# Revit family: 0048803 Sylvania Lighting Fixture HYDROPROOF LED G3 1500MM T 4K E3
name_source: partatom
category: Lighting Fixtures
revit_build: Autodesk Revit 2016 (Build: 20150220_1215(x64)
units: mm (PartAtom-declared; Revit-internal decimal feet)

## family parameters
Cut with Voids When Loaded = No
Host = Face
Light Source = Yes
OmniClass Number = 23.80.70.11.14
OmniClass Title = General Luminaries, Directional
Part Type = Normal
Room Calculation Point = No
Round Connector Dimension = Use Diameter
Shared = No

## types (2) — shared parameters
AccessoryMaterial = Diffuser-Sylvania-Glow
Assembly Code = D5020200
AssetType = Fixed
BodyMaterial = Body-Sylvania-Gray
ClassificationName = Uniclass2015
ClassificationValue = EF_70_80
Color Filter = 16777215
Default Elevation = 1219 mm
Description = Hydroproof, integrated LED chemical resistant weatherproof luminaire, with UV stabilized flat diffuser and linear prisms designed to achieve uniform lit appearance, optimise light output and to reduce glare, stainless steel diffuser clips and fixing brackets for surface and wall mounting. L 1578 mm x W 110 mm x H 78 mm size, GRP housing, PMMA diffuser, Non dimmable,   3 hour emergency, 4000K, CRI80,  6900 lm, 49 W, 140 lm/W, nominal average life (h):50000, energy class: A++ A+ A Class I,IK02, IP65.
DiffuserMaterial = Diffuser-Sylvania-Transparent
Dimming Lamp Color Temperature Shift = <None>
DimmingControlOptions = Non dimmable
DocumentationLiterature = http://www.sylvania-lighting.com
DurationUnit = hours
ElectricShockClassification = Class I
Emit Shape Visible in Rendering = No
Emit from Rectangle Length = 1552 mm  [stored 5.09186 ft]
Emit from Rectangle Width = 90 mm  [stored 0.295276 ft]
ExpectedLife = 50000
IfcExportAs = IfcLightFixtureType
IfcExportType = IfcLightFixtureType
ImpactProtectionIndex = IK02
IngressProtection = IP65
InputNominalFrequency = 50/60 Hz
InputVoltage = 220-240V~
Keynote = 16500
Lamp = LED
LampColourRenderingIndex = 80
LampColourTemperature = 4000 K
LampMacAdamStep = 3
LampsType = LED
Length = 1572 mm  [stored 5.15748 ft]
LuminousEfficacy = 140 lm/W
Manufacturer = Feilo Sylvania
ManufacturerName = Feilo Sylvania
Material = grp housing, pmma diffuser
Model = HYDROPROOF LED G3 1500MM T 4K E3
ModelNumber = 0048803
ModelReference = HYDROPROOF LED G3 1500MM T 4K E3
Name = HYDROPROOF LED G3 1500MM T 4K E3
NominalHeight = 78 mm  [stored 0.255906 ft]
NominalLength = 1578 mm  [stored 5.17717 ft]
ReflectorMaterial = <By Category>
Tilt Angle = -90.00°
Type Image = <None>
TypeName = HYDROPROOF LED G3 1500MM T 4K E3
URL = http://www.sylvania-lighting.com
Voltage = 230 V
Weight = 2.88 kg
Width = 110 mm  [stored 0.360892 ft]
zero-valued in all types: Cost, NominalWidth, PowerFactor

## per-type parameters (varying)
| type | Apparent Load | LampNominalLuminous | Photometric Web File | PowerConsumption |
| 0048803 HYDROPROOF LED G3 1500MM T 4K E3 | 49 VA | 6900 lm | 0048803.ies | 49 W |
| 0048803 HYDROPROOF LED G3 1500MM T 4K E3 Emergency mode | 2 VA | 230 lm | 0048803EM.ies | 1.64 W |

note: [stored X ft] marks values corroborated as IEEE doubles in the binary element streams (Revit-internal decimal feet)

## geometry (parser evidence)
native form markers: Sweep x4
no freeform markers — native parametric forms only
